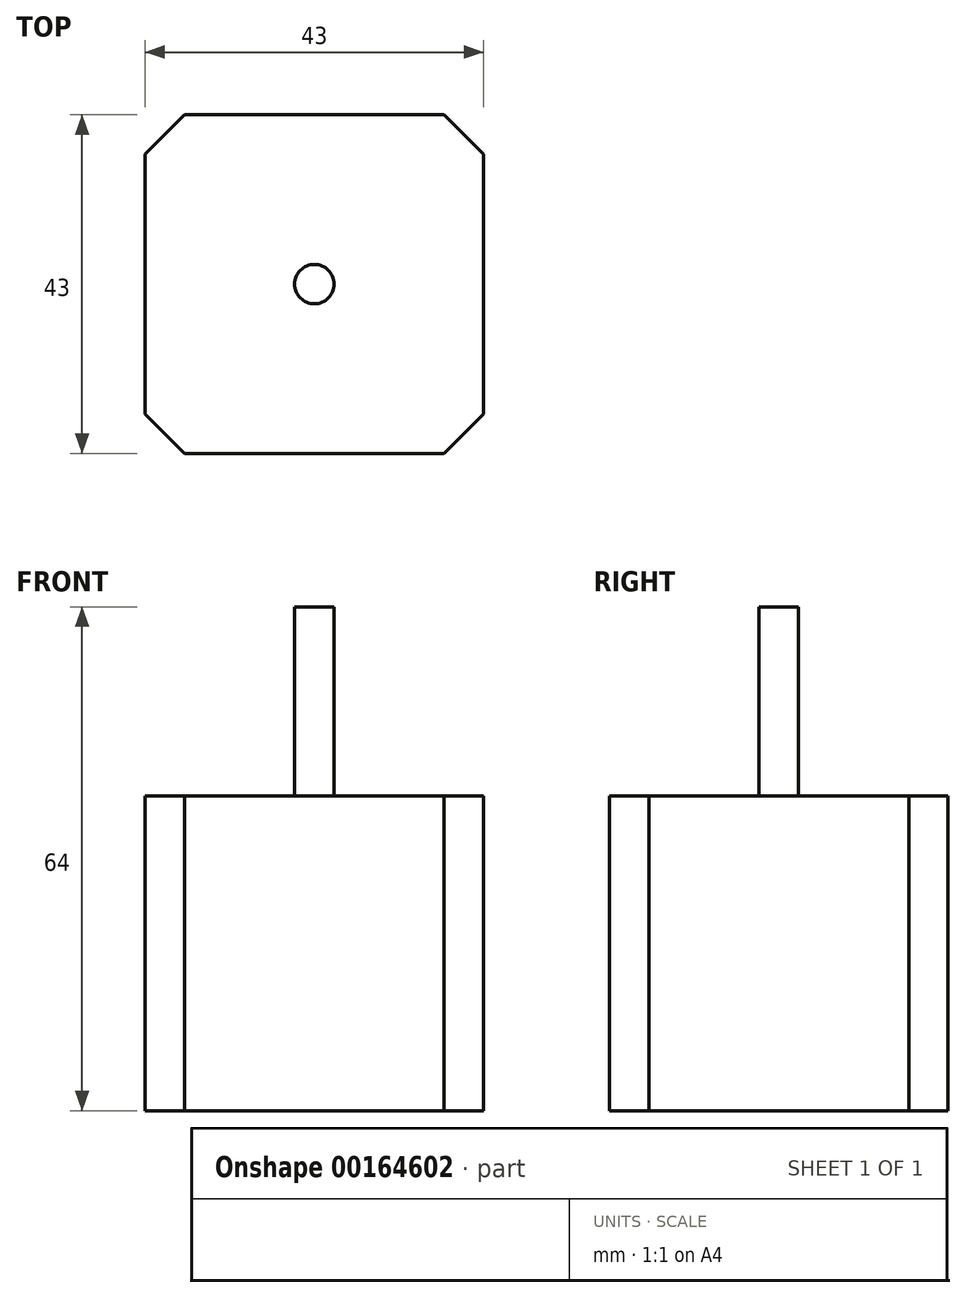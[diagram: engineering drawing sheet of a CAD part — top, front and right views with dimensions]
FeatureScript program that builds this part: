
annotation { "Feature Type Name" : "Feature", "Feature Type Description" : "" }
export const myFeature = defineFeature(function(context is Context, id is Id, definition is map)
    precondition{}
    {
        {
            var Q0;
            Q0=qCreatedBy(makeId("Top.planeOp"),FACE);
            var sketch = newSketch(context, id + "F0", { "sketchPlane" : qUnion([Q0])});
            skLineSegment(sketch, "E0.bottom", {"start": v(21.5, 21.5) * mm, "end": v(-21.5, 21.5) * mm});
            skLineSegment(sketch, "E0.top", {"start": v(21.5, -21.5) * mm, "end": v(-21.5, -21.5) * mm});
            skLineSegment(sketch, "E0.left", {"start": v(21.5, 21.5) * mm, "end": v(21.5, -21.5) * mm});
            skLineSegment(sketch, "E0.right", {"start": v(-21.5, 21.5) * mm, "end": v(-21.5, -21.5) * mm});
            skPoint(sketch, "E0.middle", {"position": v(0, 0) * mm});
            skSolve(sketch);
        }
        {
            var Q0;
            Q0 = qSketchRegion(id + "F0", true);
            extrude(context, id + "F1", {"entities" : qUnion([Q0]), "depth" : 40 * mm});
        }
        {
            var Q0;
            Q0=makeQuery(id+"F1.opExtrude","CAP_FACE",FACE,{"disambiguationData":[OSD([sQuery(id+"F0.wireOp",EDGE,"E0.bottom"),sQuery(id+"F0.wireOp",EDGE,"E0.top"),sQuery(id+"F0.wireOp",EDGE,"E0.left"),sQuery(id+"F0.wireOp",EDGE,"E0.right")])],"isStart":false});
            var sketch = newSketch(context, id + "F2", { "sketchPlane" : qUnion([Q0])});
            skCircle(sketch, "E1", {"center": v(0, 0) * mm, "radius": 2.5 * mm});
            skSolve(sketch);
        }
        {
            var Q0;
            Q0 = qSketchRegion(id + "F2", true);
            extrude(context, id + "F3", {"entities" : qUnion([Q0]), "operationType" : NewBodyOperationType.ADD, "depth" : 24 * mm});
        }
        {
            var Q0;
            Q0=makeQuery(id+"F1.opExtrude","SWEPT_EDGE",EDGE,{"disambiguationData":[OSD([sQuery(id+"F0.wireOp",EDGE,"E0.top"),sQuery(id+"F0.wireOp",EDGE,"E0.right")])]});
            var Q1;
            Q1=makeQuery(id+"F1.opExtrude","SWEPT_EDGE",EDGE,{"disambiguationData":[OSD([sQuery(id+"F0.wireOp",EDGE,"E0.top"),sQuery(id+"F0.wireOp",EDGE,"E0.left")])]});
            var Q2;
            Q2=makeQuery(id+"F1.opExtrude","SWEPT_EDGE",EDGE,{"disambiguationData":[OSD([sQuery(id+"F0.wireOp",EDGE,"E0.bottom"),sQuery(id+"F0.wireOp",EDGE,"E0.left")])]});
            var Q3;
            Q3=makeQuery(id+"F1.opExtrude","SWEPT_EDGE",EDGE,{"disambiguationData":[OSD([sQuery(id+"F0.wireOp",EDGE,"E0.bottom"),sQuery(id+"F0.wireOp",EDGE,"E0.right")])]});
            chamfer(context, id + "F4", {"entities" : qUnion([Q0, Q1, Q2, Q3]), "width" : 5 * mm, "tangentPropagation" : true});
        }
    });
